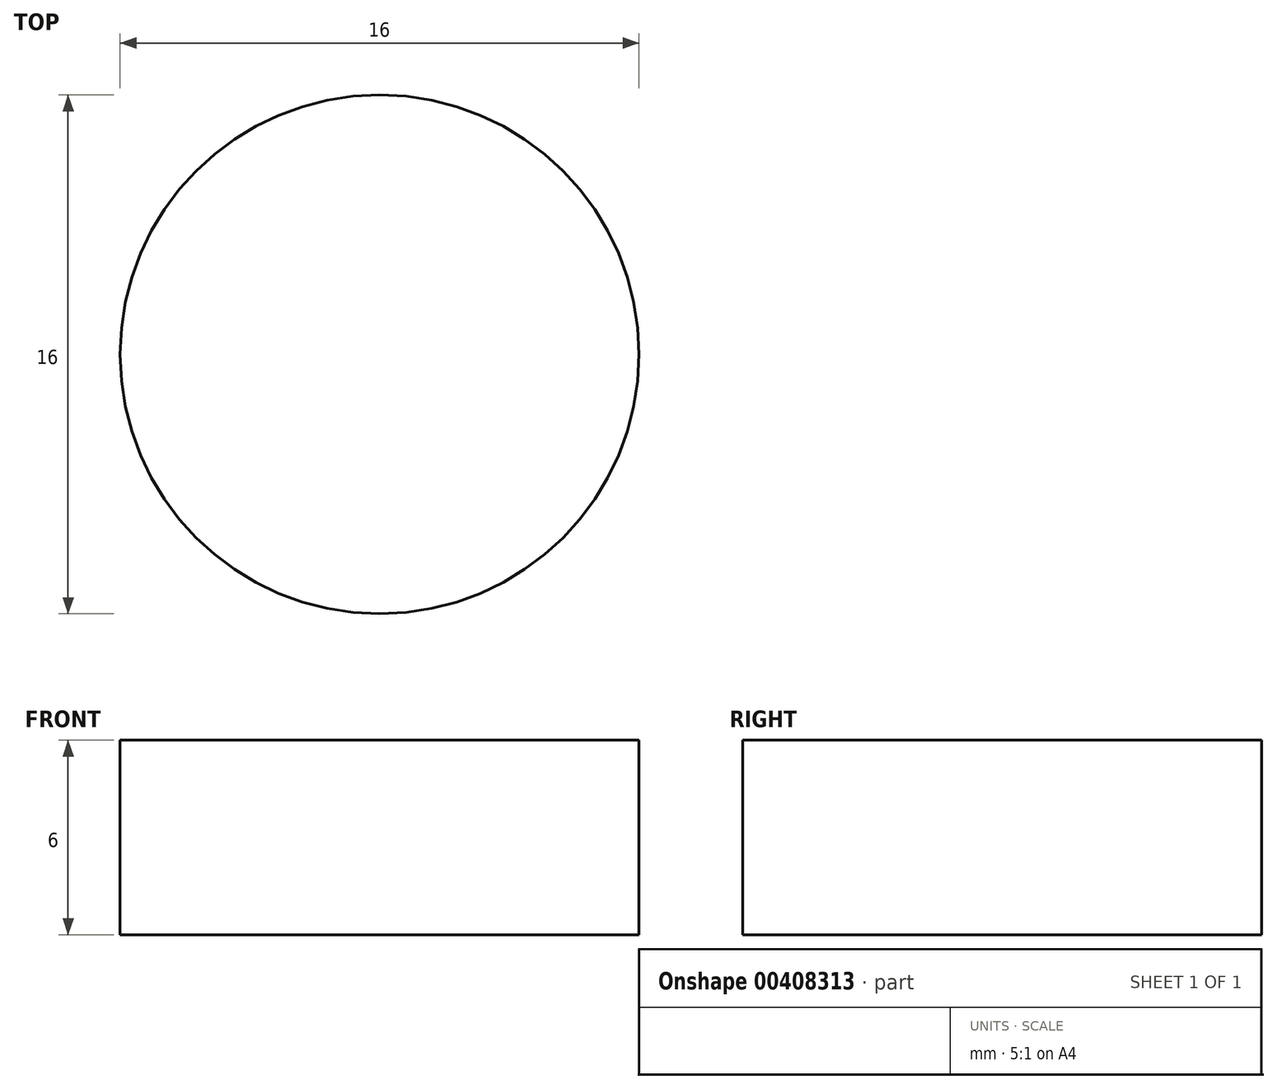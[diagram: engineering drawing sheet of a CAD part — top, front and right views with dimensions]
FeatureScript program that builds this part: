
annotation { "Feature Type Name" : "Feature", "Feature Type Description" : "" }
export const myFeature = defineFeature(function(context is Context, id is Id, definition is map)
    precondition{}
    {
        {
            var Q0;
            Q0=qCreatedBy(makeId("Top.planeOp"),FACE);
            var sketch = newSketch(context, id + "F0", { "sketchPlane" : qUnion([Q0])});
            skCircle(sketch, "E0", {"center": v(0, 0) * mm, "radius": 8 * mm});
            skSolve(sketch);
        }
        {
            var Q0;
            Q0=makeQuery(id+"F0.imprint","IMPRINT",FACE,{"disambiguationData":[TD([[makeQuery(id+"F0.imprint","IMPRINT",EDGE,{"derivedFrom":sQuery(id+"F0.wireOp",EDGE,"E0")}),1.0]])]});
            var Q1;
            Q1=sQuery(id+"F0.wireOp",EDGE,"E0");
            extrude(context, id + "F1", {"entities" : qUnion([Q0]), "bodyType" : ToolBodyType.SURFACE, "surfaceEntities" : qUnion([Q1]), "depth" : 6 * mm});
        }
    });
